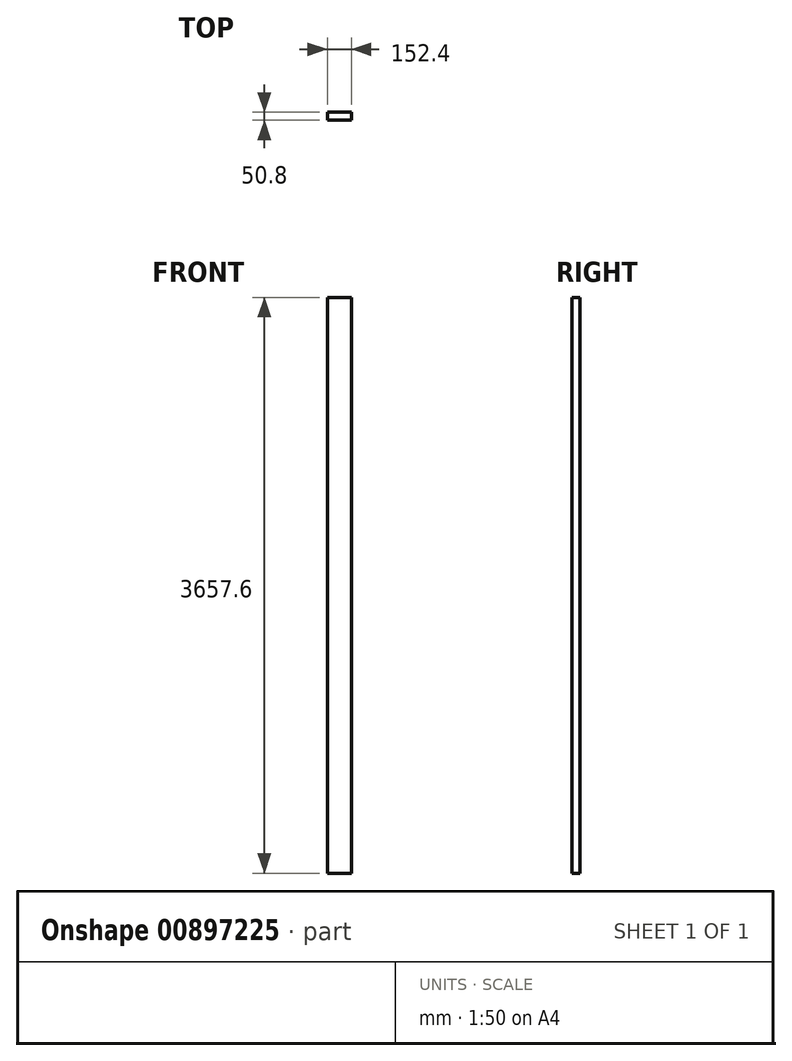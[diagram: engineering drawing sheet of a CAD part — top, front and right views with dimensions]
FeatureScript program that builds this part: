
annotation { "Feature Type Name" : "Feature", "Feature Type Description" : "" }
export const myFeature = defineFeature(function(context is Context, id is Id, definition is map)
    precondition{}
    {
        {
            var Q0;
            Q0=qCreatedBy(makeId("Top.planeOp"),FACE);
            var sketch = newSketch(context, id + "F0", { "sketchPlane" : qUnion([Q0])});
            skLineSegment(sketch, "E0.bottom", {"start": v(0, 0) * mm, "end": v(152.4, 0) * mm});
            skLineSegment(sketch, "E0.top", {"start": v(0, 50.8) * mm, "end": v(152.4, 50.8) * mm});
            skLineSegment(sketch, "E0.left", {"start": v(0, 0) * mm, "end": v(0, 50.8) * mm});
            skLineSegment(sketch, "E0.right", {"start": v(152.4, 0) * mm, "end": v(152.4, 50.8) * mm});
            skSolve(sketch);
        }
        {
            var Q0;
            Q0=qSketchRegion(id+"F0",true);
            extrude(context, id + "F1", {"entities" : qUnion([Q0]), "depth" : 3657.6 * mm, "offsetDistance" : 25.4 * mm});
        }
    });
